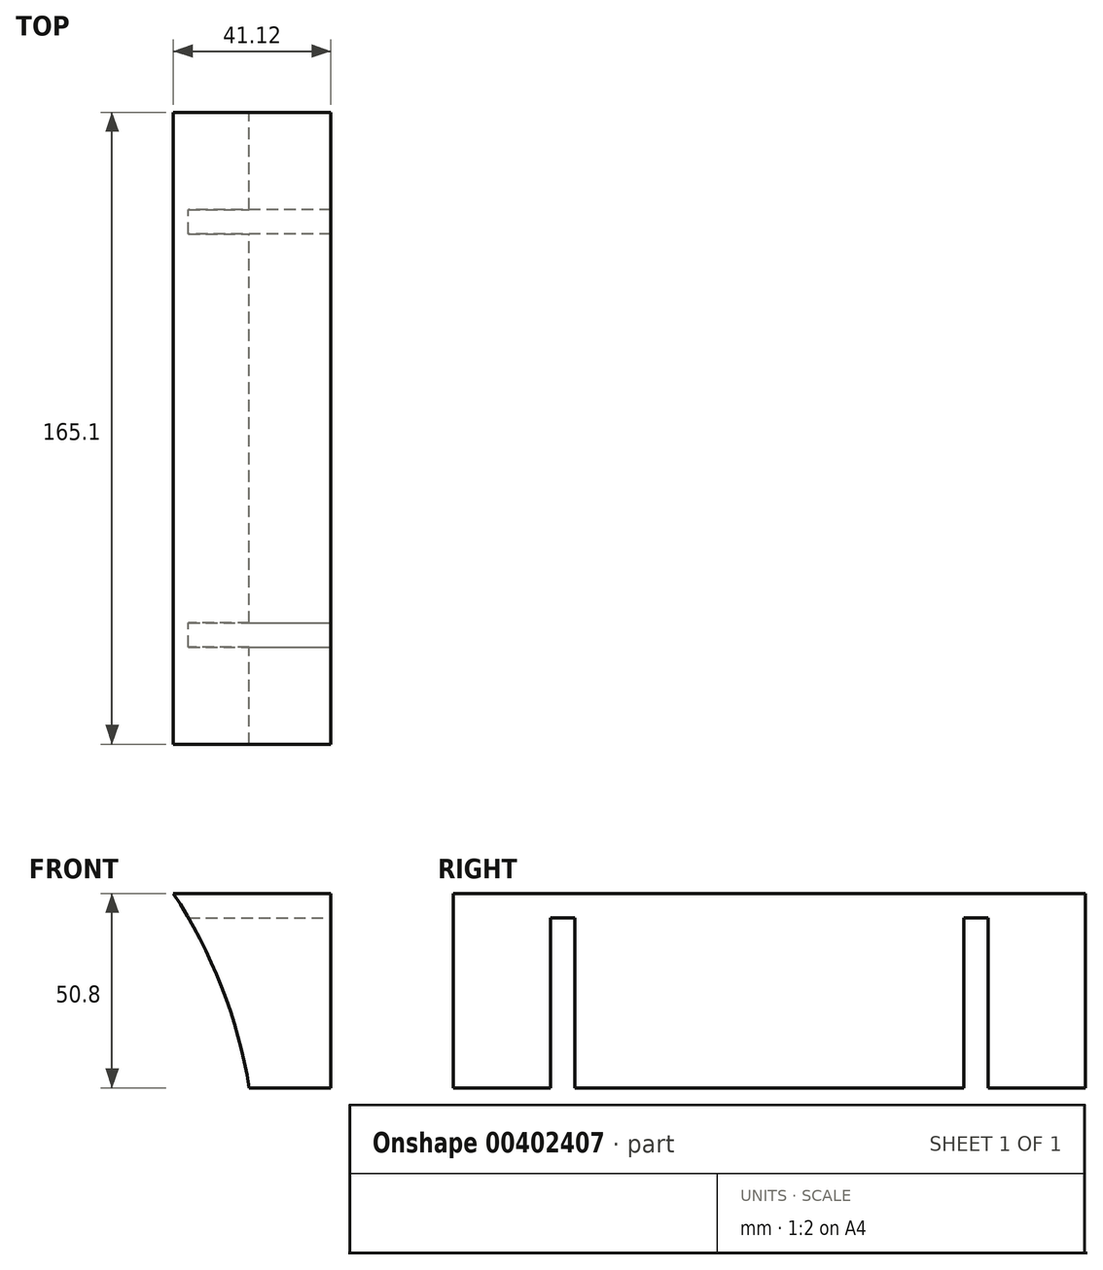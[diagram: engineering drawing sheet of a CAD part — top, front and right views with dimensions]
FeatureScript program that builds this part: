
annotation { "Feature Type Name" : "Feature", "Feature Type Description" : "" }
export const myFeature = defineFeature(function(context is Context, id is Id, definition is map)
    precondition{}
    {
        {
            var Q0;
            Q0=qCreatedBy(makeId("Front.planeOp"),FACE);
            var sketch = newSketch(context, id + "F0", { "sketchPlane" : qUnion([Q0])});
            skArc(sketch, "E0", {"start": v(75.07, 0) * mm, "mid": v(67.86, 26.45) * mm, "end": v(55.28, 50.8) * mm});
            skLineSegment(sketch, "E1", {"start": v(55.28, 50.8) * mm, "end": v(96.4, 50.8) * mm});
            skLineSegment(sketch, "E2", {"start": v(96.4, 50.8) * mm, "end": v(96.4, 0) * mm});
            skLineSegment(sketch, "E3", {"start": v(96.4, 0) * mm, "end": v(75.07, 0) * mm});
            skSolve(sketch);
        }
        {
            var Q0;
            Q0=makeQuery(id+"F0.imprint","IMPRINT",FACE,{"disambiguationData":[TD([[makeQuery(id+"F0.imprint","IMPRINT",EDGE,{"derivedFrom":sQuery(id+"F0.wireOp",EDGE,"E0")}),-1.0]])]});
            extrude(context, id + "F1", {"entities" : qUnion([Q0]), "depth" : 165.1 * mm});
        }
        {
            var Q0;
            Q0=makeQuery(id+"F1.opExtrude","CAP_FACE",FACE,{"disambiguationData":[OSD([sQuery(id+"F0.wireOp",EDGE,"E0"),sQuery(id+"F0.wireOp",EDGE,"E1"),sQuery(id+"F0.wireOp",EDGE,"E2"),sQuery(id+"F0.wireOp",EDGE,"E3")])],"isStart":false});
            cPlane(context, id + "F2", {"entities" : qUnion([Q0]), "cplaneType" : CPlaneType.OFFSET, "offset" : 25.4 * mm, "oppositeDirection" : true, "width" : 152.4 * mm, "height" : 152.4 * mm});
        }
        {
            var Q0;
            Q0=qCreatedBy(id+"F2.planeOp",FACE);
            var sketch = newSketch(context, id + "F3", { "sketchPlane" : qUnion([Q0])});
            skLineSegment(sketch, "E4.bottom", {"start": v(0, 0) * mm, "end": v(120.3, 0) * mm});
            skLineSegment(sketch, "E4.top", {"start": v(0, 44.45) * mm, "end": v(120.3, 44.45) * mm});
            skLineSegment(sketch, "E4.left", {"start": v(0, 0) * mm, "end": v(0, 44.45) * mm});
            skLineSegment(sketch, "E4.right", {"start": v(120.3, 0) * mm, "end": v(120.3, 44.45) * mm});
            skSolve(sketch);
        }
        {
            var Q0;
            Q0 = qSketchRegion(id + "F3", true);
            extrude(context, id + "F4", {"entities" : qUnion([Q0]), "operationType" : NewBodyOperationType.REMOVE, "oppositeDirection" : true, "depth" : 6.35 * mm});
        }
        {
            var Q0;
            Q0=makeQuery(id+"F1.opExtrude","CAP_FACE",FACE,{"disambiguationData":[OSD([sQuery(id+"F0.wireOp",EDGE,"E0"),sQuery(id+"F0.wireOp",EDGE,"E1"),sQuery(id+"F0.wireOp",EDGE,"E2"),sQuery(id+"F0.wireOp",EDGE,"E3")])],"isStart":true});
            cPlane(context, id + "F5", {"entities" : qUnion([Q0]), "cplaneType" : CPlaneType.OFFSET, "offset" : 25.4 * mm, "oppositeDirection" : true, "width" : 152.4 * mm, "height" : 152.4 * mm});
        }
        {
            var Q0;
            Q0=qCreatedBy(id+"F5.planeOp",FACE);
            var sketch = newSketch(context, id + "F6", { "sketchPlane" : qUnion([Q0])});
            skLineSegment(sketch, "E5.bottom", {"start": v(-105.51, 44.45) * mm, "end": v(0, 44.45) * mm});
            skLineSegment(sketch, "E5.top", {"start": v(-105.51, 0) * mm, "end": v(0, 0) * mm});
            skLineSegment(sketch, "E5.left", {"start": v(-105.51, 44.45) * mm, "end": v(-105.51, 0) * mm});
            skLineSegment(sketch, "E5.right", {"start": v(0, 44.45) * mm, "end": v(0, 0) * mm});
            skSolve(sketch);
        }
        {
            var Q0;
            Q0 = qSketchRegion(id + "F6", true);
            extrude(context, id + "F7", {"entities" : qUnion([Q0]), "operationType" : NewBodyOperationType.REMOVE, "oppositeDirection" : true, "depth" : 6.35 * mm});
        }
    });
